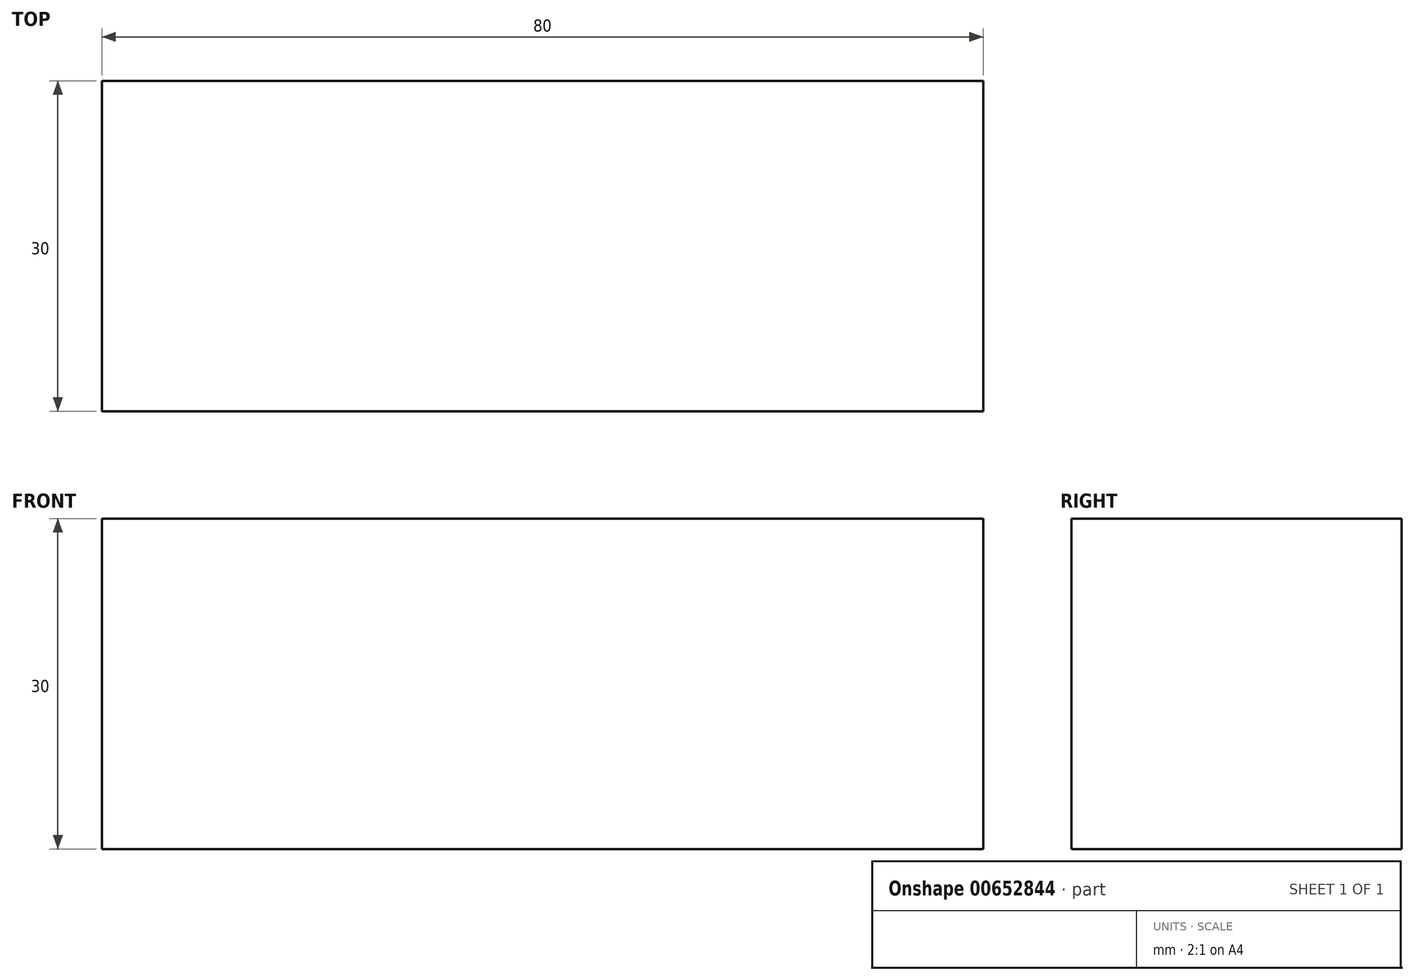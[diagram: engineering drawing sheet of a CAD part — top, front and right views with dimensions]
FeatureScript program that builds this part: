
annotation { "Feature Type Name" : "Feature", "Feature Type Description" : "" }
export const myFeature = defineFeature(function(context is Context, id is Id, definition is map)
    precondition{}
    {
        {
            var Q0;
            Q0=qCreatedBy(makeId("Front.planeOp"),FACE);
            var sketch = newSketch(context, id + "F0", { "sketchPlane" : qUnion([Q0])});
            skLineSegment(sketch, "E0.bottom", {"start": v(-40, 15) * mm, "end": v(40, 15) * mm});
            skLineSegment(sketch, "E0.top", {"start": v(-40, -15) * mm, "end": v(40, -15) * mm});
            skLineSegment(sketch, "E0.left", {"start": v(-40, 15) * mm, "end": v(-40, -15) * mm});
            skLineSegment(sketch, "E0.right", {"start": v(40, 15) * mm, "end": v(40, -15) * mm});
            skPoint(sketch, "E0.middle", {"position": v(0, 0) * mm});
            skSolve(sketch);
        }
        {
            var Q0;
            Q0 = qSketchRegion(id + "F0", true);
            extrude(context, id + "F1", {"entities" : qUnion([Q0]), "depth" : 30 * mm, "offsetDistance" : 25 * mm});
        }
    });
